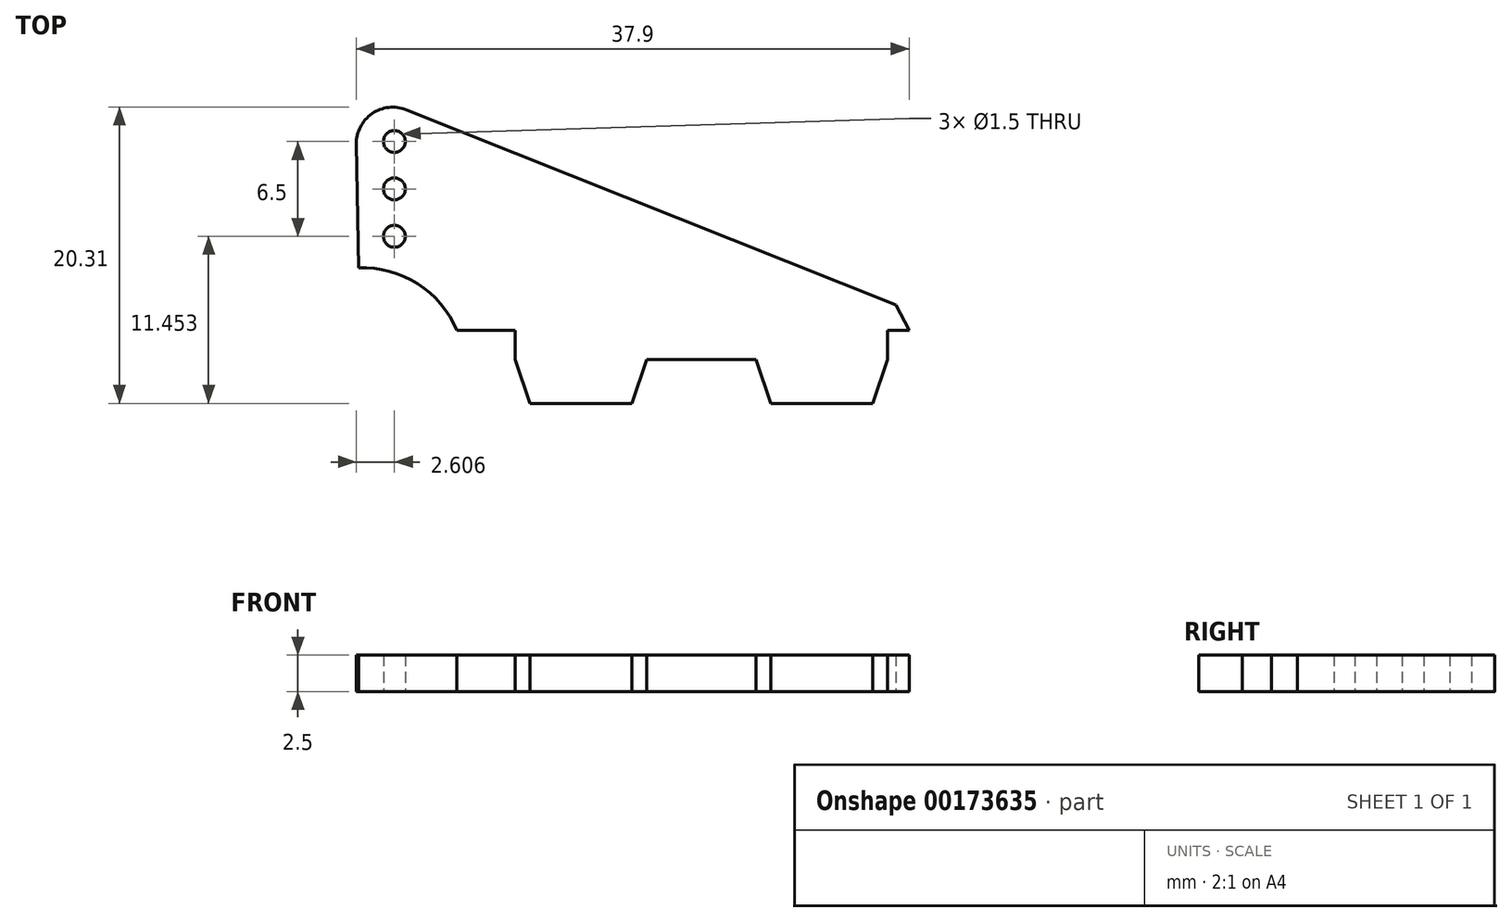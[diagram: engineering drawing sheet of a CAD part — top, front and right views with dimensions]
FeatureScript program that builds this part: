
annotation { "Feature Type Name" : "Feature", "Feature Type Description" : "" }
export const myFeature = defineFeature(function(context is Context, id is Id, definition is map)
    precondition{}
    {
        {
            var Q0;
            Q0=qCreatedBy(makeId("Top.planeOp"),FACE);
            var sketch = newSketch(context, id + "F0", { "sketchPlane" : qUnion([Q0])});
            skLineSegment(sketch, "E0", {"start": v(-26.54, 19.71) * mm, "end": v(4.46, 19.71) * mm, "construction": true});
            skCircle(sketch, "E1", {"center": v(4.46, 19.71) * mm, "radius": 1.5 * mm, "construction": true});
            skCircle(sketch, "E2", {"center": v(-26.54, 19.71) * mm, "radius": 4 * mm, "construction": true});
            skCircle(sketch, "E3", {"center": v(-26.54, 19.71) * mm, "radius": 17 * mm, "construction": true});
            skCircle(sketch, "E4", {"center": v(4.46, 19.71) * mm, "radius": 41 * mm, "construction": true});
            skLineSegment(sketch, "E5", {"start": v(3.56, 21.47) * mm, "end": v(4.46, 19.71) * mm});
            skLineSegment(sketch, "E6", {"start": v(4.46, 19.71) * mm, "end": v(2.96, 19.71) * mm});
            skLineSegment(sketch, "E7", {"start": v(-26.54, 19.71) * mm, "end": v(-22.54, 19.71) * mm});
            skCircle(sketch, "E8", {"center": v(-26.54, 19.71) * mm, "radius": 8 * mm, "construction": true});
            skCircle(sketch, "E9", {"center": v(4.46, 19.71) * mm, "radius": 38 * mm, "construction": true});
            skLineSegment(sketch, "E10", {"start": v(-33.3, 24) * mm, "end": v(-33.44, 32.47) * mm});
            skPoint(sketch, "E11.visualSharp", {"position": v(-33.49, 35.23) * mm});
            skArc(sketch, "E12", {"start": v(-26.54, 19.71) * mm, "mid": v(-29.24, 22.92) * mm, "end": v(-33.3, 24) * mm});
            skLineSegment(sketch, "E13", {"start": v(-22.54, 19.71) * mm, "end": v(-22.54, 17.71) * mm});
            skLineSegment(sketch, "E14", {"start": v(-22.54, 17.71) * mm, "end": v(-22.54, 14.71) * mm, "construction": true});
            skLineSegment(sketch, "E15", {"start": v(-22.54, 14.71) * mm, "end": v(8.64, 14.71) * mm, "construction": true});
            skLineSegment(sketch, "E16", {"start": v(2.96, 19.71) * mm, "end": v(2.96, 17.71) * mm});
            skLineSegment(sketch, "E17", {"start": v(2.96, 17.71) * mm, "end": v(1.96, 17.71) * mm, "construction": true});
            skLineSegment(sketch, "E18", {"start": v(1.96, 17.71) * mm, "end": v(1.96, 13.58) * mm, "construction": true});
            skLineSegment(sketch, "E19", {"start": v(2.96, 17.71) * mm, "end": v(1.96, 14.71) * mm});
            skLineSegment(sketch, "E20", {"start": v(1.96, 14.71) * mm, "end": v(-5.04, 14.71) * mm});
            skLineSegment(sketch, "E21", {"start": v(-5.04, 14.71) * mm, "end": v(-5.04, 17.71) * mm, "construction": true});
            skLineSegment(sketch, "E22", {"start": v(-5.04, 17.71) * mm, "end": v(-6.04, 17.71) * mm, "construction": true});
            skLineSegment(sketch, "E23", {"start": v(-5.04, 14.71) * mm, "end": v(-6.04, 17.71) * mm});
            skLineSegment(sketch, "E24", {"start": v(-22.54, 17.71) * mm, "end": v(-21.54, 17.71) * mm, "construction": true});
            skLineSegment(sketch, "E25", {"start": v(-21.54, 17.71) * mm, "end": v(-21.54, 14.71) * mm, "construction": true});
            skLineSegment(sketch, "E26", {"start": v(-22.54, 17.71) * mm, "end": v(-21.54, 14.71) * mm});
            skLineSegment(sketch, "E27", {"start": v(-21.54, 14.71) * mm, "end": v(-14.54, 14.71) * mm});
            skLineSegment(sketch, "E28", {"start": v(-14.54, 14.71) * mm, "end": v(-14.54, 17.71) * mm, "construction": true});
            skLineSegment(sketch, "E29", {"start": v(-14.54, 17.71) * mm, "end": v(-13.54, 17.71) * mm, "construction": true});
            skLineSegment(sketch, "E30", {"start": v(-14.54, 14.71) * mm, "end": v(-13.54, 17.71) * mm});
            skLineSegment(sketch, "E31", {"start": v(-13.54, 17.71) * mm, "end": v(-6.04, 17.71) * mm});
            skLineSegment(sketch, "E32", {"start": v(-33.33, 26.16) * mm, "end": v(-30.83, 26.2) * mm, "construction": true});
            skLineSegment(sketch, "E33", {"start": v(-30.83, 23.66) * mm, "end": v(-30.83, 36.97) * mm, "construction": true});
            skCircle(sketch, "E34", {"center": v(-30.83, 23.66) * mm, "radius": 2.5 * mm, "construction": true});
            skCircle(sketch, "E35", {"center": v(-30.83, 26.16) * mm, "radius": 0.75 * mm});
            skCircle(sketch, "E36", {"center": v(-30.83, 26.16) * mm, "radius": 3.25 * mm, "construction": true});
            skCircle(sketch, "E37", {"center": v(-30.83, 29.41) * mm, "radius": 0.75 * mm});
            skCircle(sketch, "E38", {"center": v(-30.83, 29.41) * mm, "radius": 3.25 * mm, "construction": true});
            skCircle(sketch, "E39", {"center": v(-30.83, 32.66) * mm, "radius": 0.75 * mm});
            skCircle(sketch, "E40", {"center": v(-30.83, 32.66) * mm, "radius": 2.5 * mm, "construction": true});
            skLineSegment(sketch, "E41", {"start": v(3.56, 21.47) * mm, "end": v(-30.02, 34.84) * mm});
            skPoint(sketch, "E42.visualSharp", {"position": v(-33.5, 36.23) * mm});
            skArc(sketch, "E42.filletArc", {"start": v(-30.02, 34.84) * mm, "mid": v(-32.36, 34.57) * mm, "end": v(-33.44, 32.47) * mm});
            skSolve(sketch);
        }
        {
            var Q0;
            Q0=makeQuery(id+"F0.imprint","IMPRINT",FACE,{"disambiguationData":[TD([[makeQuery(id+"F0.imprint","IMPRINT",EDGE,{"derivedFrom":sQuery(id+"F0.wireOp",EDGE,"E5")}),-1.0]])]});
            extrude(context, id + "F1", {"entities" : qUnion([Q0]), "depth" : 2.5 * mm});
        }
    });
